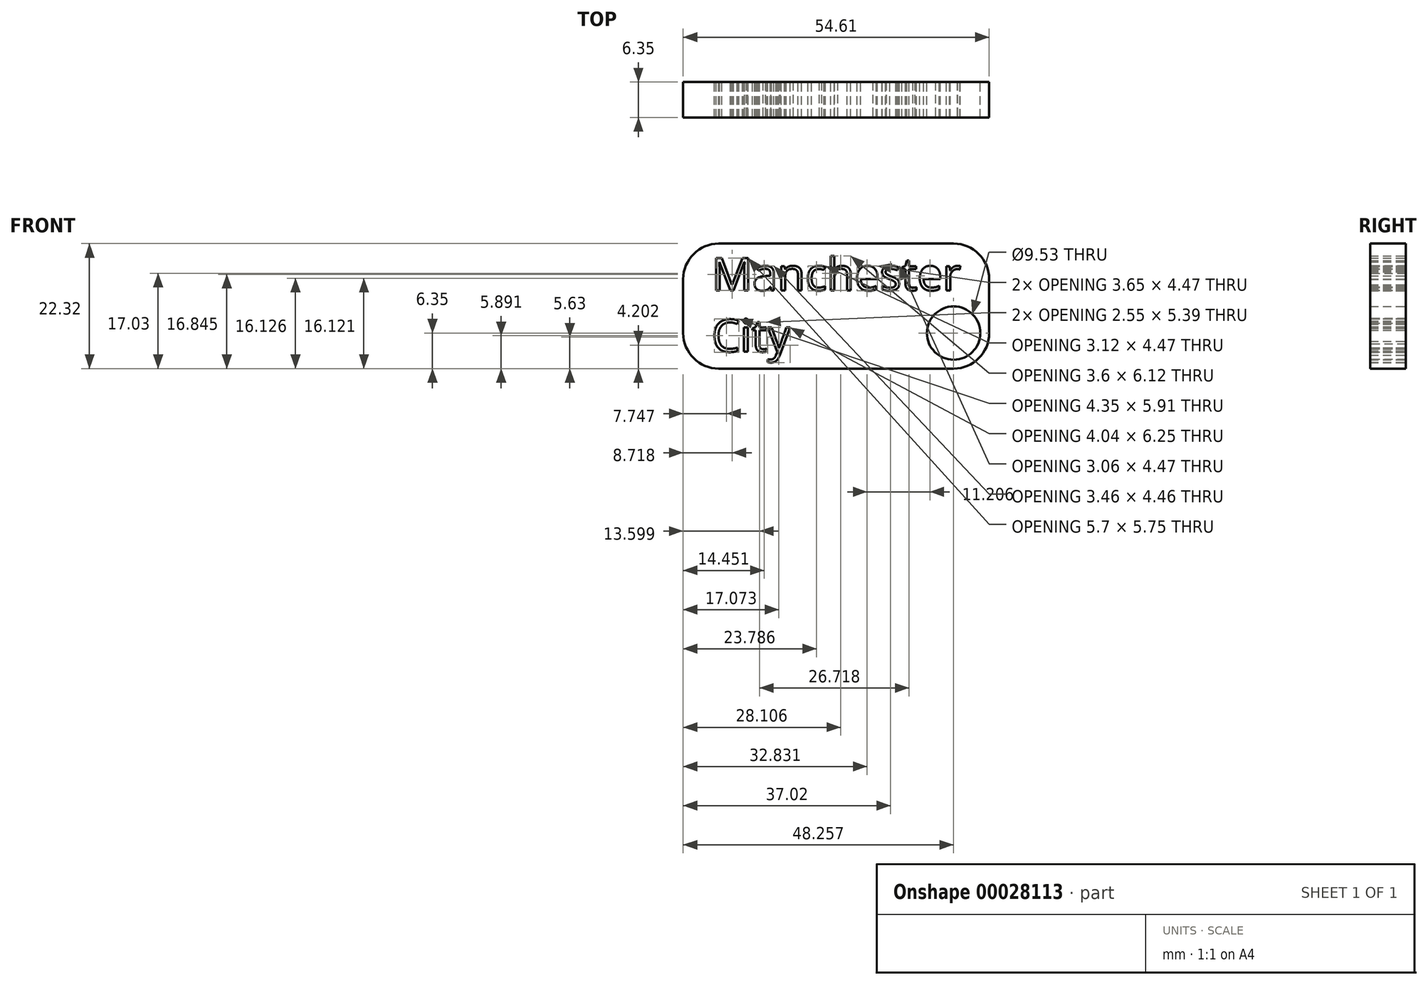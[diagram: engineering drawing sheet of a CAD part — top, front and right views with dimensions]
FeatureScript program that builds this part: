
annotation { "Feature Type Name" : "Feature", "Feature Type Description" : "" }
export const myFeature = defineFeature(function(context is Context, id is Id, definition is map)
    precondition{}
    {
        {
            var Q0;
            Q0=qCreatedBy(makeId("Front.planeOp"),FACE);
            var sketch = newSketch(context, id + "F0", { "sketchPlane" : qUnion([Q0])});
            skText(sketch, "E0", { "text": "Manchester\nCity", "fontName": "OpenSans-Regular.ttf"});
            skLineSegment(sketch, "E1.bottom", {"start": v(-6.83, 8.35) * mm, "end": v(35.08, 8.35) * mm});
            skLineSegment(sketch, "E1.top", {"start": v(-6.83, -13.97) * mm, "end": v(35.08, -13.97) * mm});
            skLineSegment(sketch, "E1.left", {"start": v(-13.18, 2) * mm, "end": v(-13.18, -7.62) * mm});
            skLineSegment(sketch, "E1.right", {"start": v(41.43, 2) * mm, "end": v(41.43, -7.62) * mm});
            skPoint(sketch, "E2.visualSharp", {"position": v(-13.18, 8.35) * mm});
            skArc(sketch, "E2.filletArc", {"start": v(-6.83, 8.35) * mm, "mid": v(-11.32, 6.49) * mm, "end": v(-13.18, 2) * mm});
            skPoint(sketch, "E3.visualSharp", {"position": v(41.43, 8.35) * mm});
            skArc(sketch, "E3.filletArc", {"start": v(41.43, 2) * mm, "mid": v(39.57, 6.49) * mm, "end": v(35.08, 8.35) * mm});
            skPoint(sketch, "E4.visualSharp", {"position": v(41.43, -13.97) * mm});
            skArc(sketch, "E4.filletArc", {"start": v(35.08, -13.97) * mm, "mid": v(39.57, -12.11) * mm, "end": v(41.43, -7.62) * mm});
            skPoint(sketch, "E5.visualSharp", {"position": v(-13.18, -13.97) * mm});
            skArc(sketch, "E5.filletArc", {"start": v(-13.18, -7.62) * mm, "mid": v(-11.32, -12.11) * mm, "end": v(-6.83, -13.97) * mm});
            skCircle(sketch, "E6", {"center": v(35.08, -7.62) * mm, "radius": 4.76 * mm});
            const initialGuessF0  = {"E0": [-0.0081, 0, 1, 0, 0.0058]};
            skSetInitialGuess(sketch, initialGuessF0);
            skSolve(sketch);
        }
        {
            var Q0;
            Q0=makeQuery(id+"F0.imprint","IMPRINT",FACE,{"disambiguationData":[TD([[makeQuery(id+"F0.imprint","IMPRINT",EDGE,{"derivedFrom":sQuery(id+"F0.wireOp",EDGE,"E0.sketch_text.stroke-0")}),1.0]])]});
            extrude(context, id + "F1", {"entities" : qUnion([Q0]), "depth" : 6.35 * mm});
        }
    });
